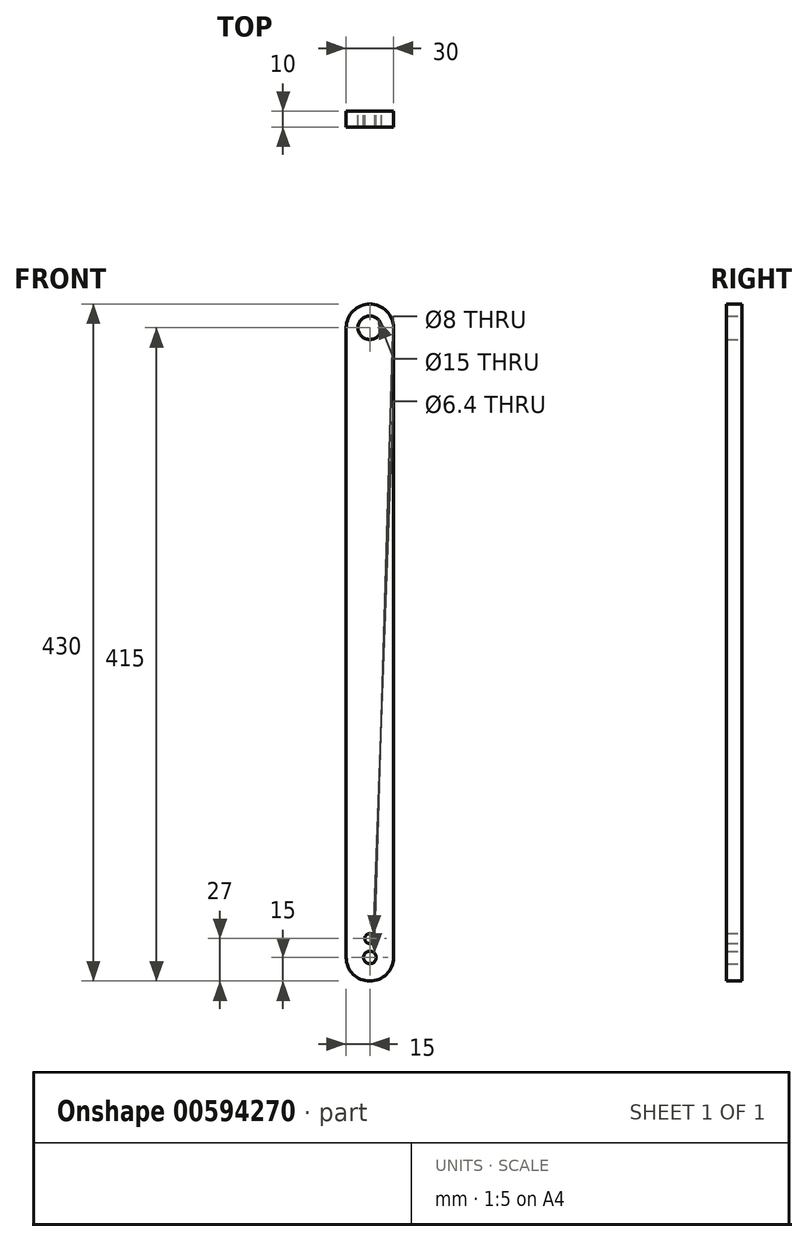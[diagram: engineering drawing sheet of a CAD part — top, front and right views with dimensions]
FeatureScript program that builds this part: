
annotation { "Feature Type Name" : "Feature", "Feature Type Description" : "" }
export const myFeature = defineFeature(function(context is Context, id is Id, definition is map)
    precondition{}
    {
        {
            var Q0;
            Q0=qCreatedBy(makeId("Front.planeOp"),FACE);
            var sketch = newSketch(context, id + "F0", { "sketchPlane" : qUnion([Q0])});
            skLineSegment(sketch, "E0", {"start": v(0, 0) * mm, "end": v(0, 400) * mm, "construction": true});
            skCircle(sketch, "E1", {"center": v(0, 400) * mm, "radius": 7.5 * mm});
            skCircle(sketch, "E2", {"center": v(0, 0) * mm, "radius": 4 * mm});
            skArc(sketch, "E3", {"start": v(-15, 0) * mm, "mid": v(0, -15) * mm, "end": v(15, 0) * mm});
            skArc(sketch, "E4", {"start": v(15, 400) * mm, "mid": v(0, 415) * mm, "end": v(-15, 400) * mm});
            skLineSegment(sketch, "E5", {"start": v(0, 400) * mm, "end": v(-15, 400) * mm, "construction": true});
            skLineSegment(sketch, "E6", {"start": v(0, 0) * mm, "end": v(-15, 0) * mm, "construction": true});
            skLineSegment(sketch, "E7", {"start": v(-15, 0) * mm, "end": v(-15, 400) * mm});
            skLineSegment(sketch, "E8.MirrorCS", {"start": v(15, 0) * mm, "end": v(15, 400) * mm});
            skCircle(sketch, "E9", {"center": v(0, 12) * mm, "radius": 3.2 * mm});
            skSolve(sketch);
        }
        {
            var Q0;
            Q0=makeQuery(id+"F0.imprint","IMPRINT",FACE,{"disambiguationData":[TD([[makeQuery(id+"F0.imprint","IMPRINT",EDGE,{"derivedFrom":sQuery(id+"F0.wireOp",EDGE,"E1")}),-1.0]])]});
            extrude(context, id + "F1", {"entities" : qUnion([Q0]), "depth" : 10 * mm, "offsetDistance" : 25 * mm});
        }
    });
